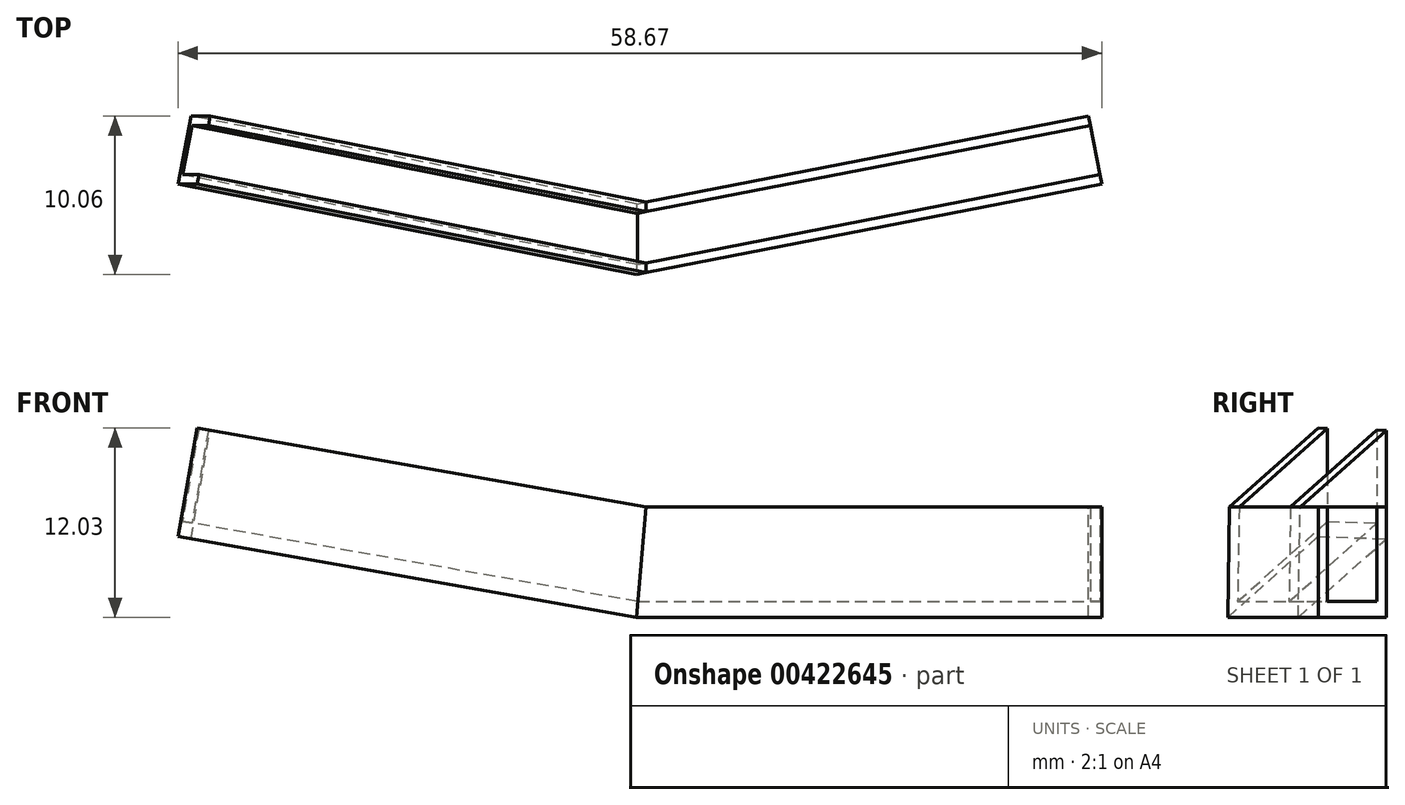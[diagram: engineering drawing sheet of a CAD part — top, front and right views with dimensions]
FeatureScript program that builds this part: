
annotation { "Feature Type Name" : "Feature", "Feature Type Description" : "" }
export const myFeature = defineFeature(function(context is Context, id is Id, definition is map)
    precondition{}
    {
        {
            var Q0;
            Q0=qCreatedBy(makeId("Top.planeOp"),FACE);
            var sketch = newSketch(context, id + "F0", { "sketchPlane" : qUnion([Q0])});
            skLineSegment(sketch, "E0", {"start": v(0, 0) * mm, "end": v(29.45, 5.72) * mm});
            skLineSegment(sketch, "E1", {"start": v(0, 0) * mm, "end": v(0, 30.95) * mm, "construction": true});
            skLineSegment(sketch, "E2.MirrorCS", {"start": v(0, 0) * mm, "end": v(-29.45, 5.72) * mm});
            skLineSegment(sketch, "E3", {"start": v(-29.45, 5.72) * mm, "end": v(-28.84, 8.87) * mm});
            skLineSegment(sketch, "E4", {"start": v(29.45, 5.72) * mm, "end": v(28.84, 8.87) * mm});
            skLineSegment(sketch, "E5", {"start": v(-28.84, 8.87) * mm, "end": v(0, 3.26) * mm});
            skLineSegment(sketch, "E6", {"start": v(0, 3.26) * mm, "end": v(28.84, 8.87) * mm});
            skLineSegment(sketch, "E7", {"start": v(-29.45, 5.72) * mm, "end": v(-29.56, 5.14) * mm});
            skLineSegment(sketch, "E8", {"start": v(-29.56, 5.14) * mm, "end": v(0, -0.61) * mm});
            skLineSegment(sketch, "E9", {"start": v(0, -0.61) * mm, "end": v(29.56, 5.14) * mm});
            skLineSegment(sketch, "E10", {"start": v(29.56, 5.14) * mm, "end": v(29.45, 5.72) * mm});
            skLineSegment(sketch, "E11", {"start": v(-28.84, 8.87) * mm, "end": v(-28.72, 9.45) * mm});
            skLineSegment(sketch, "E12", {"start": v(-28.72, 9.45) * mm, "end": v(0, 3.87) * mm});
            skLineSegment(sketch, "E13", {"start": v(0, 3.87) * mm, "end": v(28.72, 9.45) * mm});
            skLineSegment(sketch, "E14", {"start": v(28.72, 9.45) * mm, "end": v(28.84, 8.87) * mm});
            skSolve(sketch);
        }
        {
            var Q0;
            Q0=qSketchRegion(id+"F0",true);
            extrude(context, id + "F1", {"entities" : qUnion([Q0]), "oppositeDirection" : true, "depth" : 1 * mm});
        }
        {
            var Q0;
            Q0=makeQuery(id+"F0.imprint","IMPRINT",FACE,{"disambiguationData":[TD([[makeQuery(id+"F0.imprint","IMPRINT",EDGE,{"derivedFrom":sQuery(id+"F0.wireOp",EDGE,"E5")}),1.0]])]});
            var Q1;
            Q1=makeQuery(id+"F0.imprint","IMPRINT",FACE,{"disambiguationData":[TD([[makeQuery(id+"F0.imprint","IMPRINT",EDGE,{"derivedFrom":sQuery(id+"F0.wireOp",EDGE,"E0")}),-1.0]])]});
            extrude(context, id + "F2", {"entities" : qUnion([Q0, Q1]), "operationType" : NewBodyOperationType.ADD, "depth" : 6 * mm});
        }
        {
            var Q0;
            {var subQ0=sQuery(id+"F0.wireOp",EDGE,"E13");Q0=makeQuery(id+"F2.boolean.opBoolean","MERGE",FACE,{"derivedFrom":[makeQuery(id+"F1.opExtrude","SWEPT_FACE",FACE,{"disambiguationData":[OSD([subQ0])]}),makeQuery(id+"F2.opExtrude","SWEPT_FACE",FACE,{"disambiguationData":[OSD([subQ0])]})]});}
            var sketch = newSketch(context, id + "F3", { "sketchPlane" : qUnion([Q0])});
            skLineSegment(sketch, "E15", {"start": v(-30, 6) * mm, "end": v(-30, 2) * mm});
            skLineSegment(sketch, "E16", {"start": v(-30, 6) * mm, "end": v(-8.74, 6) * mm});
            skLineSegment(sketch, "E17", {"start": v(-8.74, 6) * mm, "end": v(-30, 2) * mm});
            skSolve(sketch);
        }
        {
            var Q0;
            {var subQ0=sQuery(id+"F0.wireOp",EDGE,"E12");Q0=makeQuery(id+"F2.boolean.opBoolean","MERGE",FACE,{"derivedFrom":[makeQuery(id+"F1.opExtrude","SWEPT_FACE",FACE,{"disambiguationData":[OSD([subQ0])]}),makeQuery(id+"F2.opExtrude","SWEPT_FACE",FACE,{"disambiguationData":[OSD([subQ0])]})]});}
            var sketch = newSketch(context, id + "F4", { "sketchPlane" : qUnion([Q0])});
            skLineSegment(sketch, "E18", {"start": v(30, 6) * mm, "end": v(8.74, 6) * mm});
            skLineSegment(sketch, "E19", {"start": v(8.74, 6) * mm, "end": v(30, 2) * mm});
            skLineSegment(sketch, "E20", {"start": v(30, 2) * mm, "end": v(30, 6) * mm});
            skSolve(sketch);
        }
        {
            var Q0;
            Q0=qSketchRegion(id+"F4",true);
            extrude(context, id + "F5", {"entities" : qUnion([Q0]), "operationType" : NewBodyOperationType.REMOVE, "oppositeDirection" : true, "depth" : 25 * mm});
        }
        {
            var Q0;
            Q0=qCreatedBy(makeId("Front.planeOp"),FACE);
            cPlane(context, id + "F6", {"entities" : qUnion([Q0]), "cplaneType" : CPlaneType.OFFSET, "offset" : 10 * mm, "width" : 150 * mm, "height" : 150 * mm});
        }
        {
            var Q0;
            Q0=qCreatedBy(id+"F6.planeOp",FACE);
            var sketch = newSketch(context, id + "F7", { "sketchPlane" : qUnion([Q0])});
            skLineSegment(sketch, "E21.bottom", {"start": v(0, -2.25) * mm, "end": v(-30.25, -2.25) * mm});
            skLineSegment(sketch, "E21.top", {"start": v(0, 10.58) * mm, "end": v(-30.25, 10.58) * mm});
            skLineSegment(sketch, "E21.left", {"start": v(0, -2.25) * mm, "end": v(0, 10.58) * mm});
            skLineSegment(sketch, "E21.right", {"start": v(-30.25, -2.25) * mm, "end": v(-30.25, 10.58) * mm});
            skLineSegment(sketch, "E22", {"start": v(0, -1) * mm, "end": v(1.06, 11.11) * mm});
            skLineSegment(sketch, "E23", {"start": v(1.06, 11.11) * mm, "end": v(0, 10.58) * mm});
            skSolve(sketch);
        }
        {
            var Q0;
            Q0=makeQuery(id+"F7.imprint","IMPRINT",FACE,{"disambiguationData":[TD([[makeQuery(id+"F7.imprint","IMPRINT",EDGE,{"derivedFrom":sQuery(id+"F7.wireOp",EDGE,"E21.bottom")}),-1.0]])]});
            var Q1;
            {var subQ2=sQuery(id+"F7.wireOp",EDGE,"E22");Q1=makeQuery(id+"F7.imprint","IMPRINT",FACE,{"disambiguationData":[TD([[makeQuery(id+"F7.imprint","IMPRINT",EDGE,{"derivedFrom":subQ2}),1.0]])]});}
            extrude(context, id + "F8", {"entities" : qUnion([Q0, Q1]), "operationType" : NewBodyOperationType.REMOVE, "endBound" : BoundingType.THROUGH_ALL, "oppositeDirection" : true, "depth" : 25 * mm});
        }
        {
            var Q0;
            Q0=makeQuery(id+"F8.boolean.opBoolean","COPY",FACE,{"derivedFrom":makeQuery(id+"F8.opExtrude","SWEPT_FACE",FACE,{"disambiguationData":[OSD([sQuery(id+"F7.wireOp",EDGE,"E22")])]})});
            cPlane(context, id + "F9", {"entities" : qUnion([Q0]), "cplaneType" : CPlaneType.OFFSET, "offset" : 0 * mm, "width" : 150 * mm, "height" : 150 * mm});
        }
        {
            var Q0;
            Q0=makeQuery(id+"F1.opExtrude","SWEPT_BODY",BODY,{"disambiguationData":[OSD([sQuery(id+"F0.wireOp",EDGE,"E3"),sQuery(id+"F0.wireOp",EDGE,"E4"),sQuery(id+"F0.wireOp",EDGE,"E7"),sQuery(id+"F0.wireOp",EDGE,"E8"),sQuery(id+"F0.wireOp",EDGE,"E9"),sQuery(id+"F0.wireOp",EDGE,"E10"),sQuery(id+"F0.wireOp",EDGE,"E11"),sQuery(id+"F0.wireOp",EDGE,"E12"),sQuery(id+"F0.wireOp",EDGE,"E13"),sQuery(id+"F0.wireOp",EDGE,"E14")])]});
            var Q1;
            Q1=qCreatedBy(id+"F9.planeOp",FACE);
            mirror(context, id + "F10", {"operationType" : NewBodyOperationType.ADD, "entities" : qUnion([Q0]), "mirrorPlane" : qUnion([Q1])});
        }
    });
